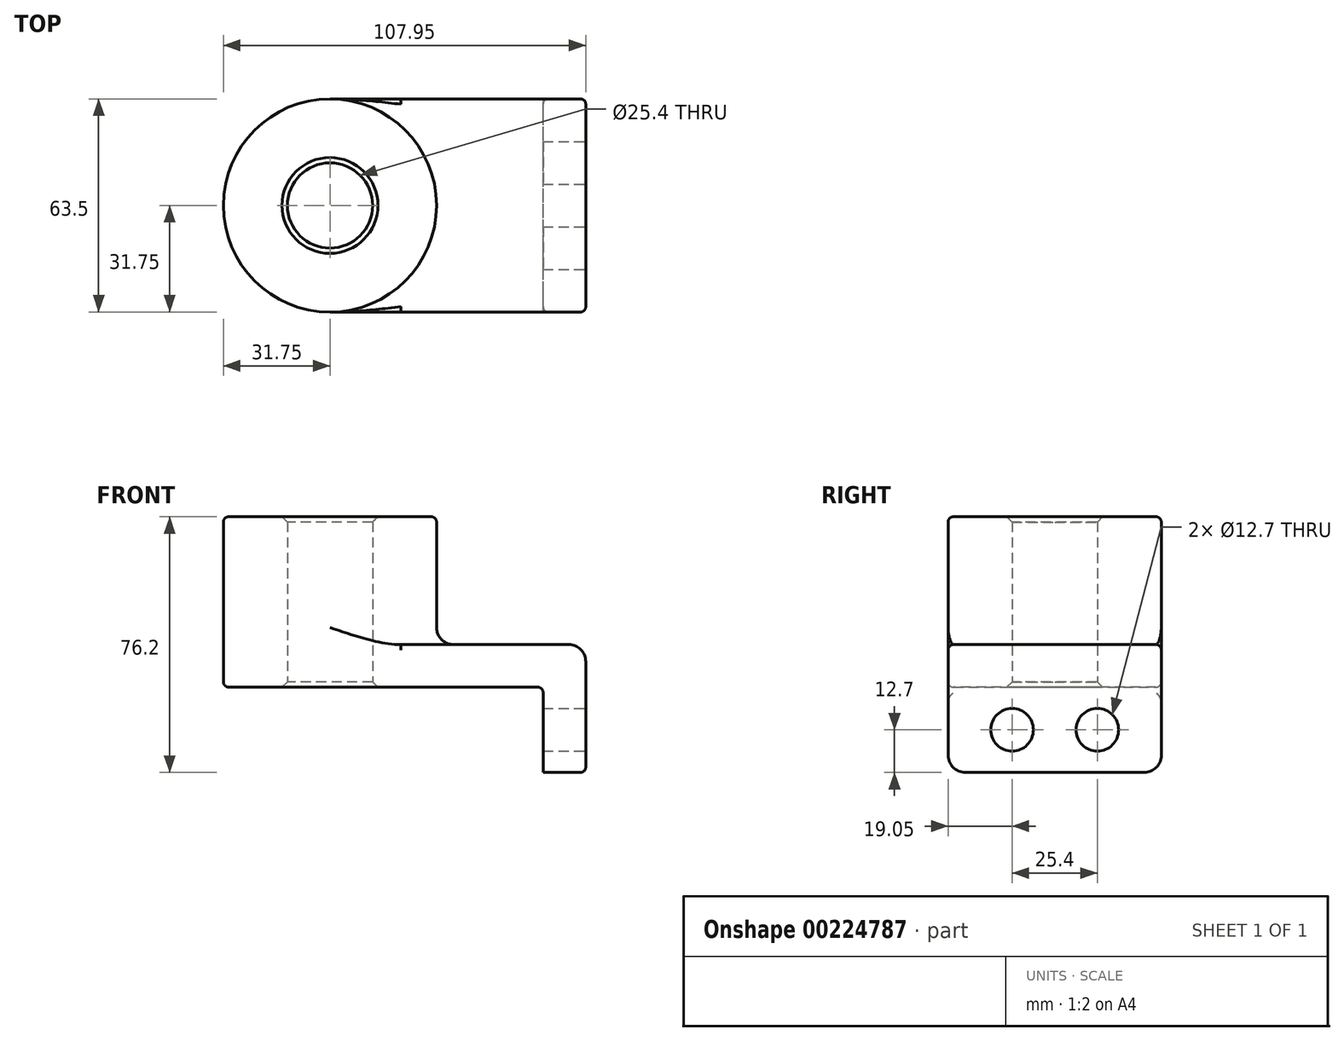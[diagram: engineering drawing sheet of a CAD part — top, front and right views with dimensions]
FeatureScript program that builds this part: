
annotation { "Feature Type Name" : "Feature", "Feature Type Description" : "" }
export const myFeature = defineFeature(function(context is Context, id is Id, definition is map)
    precondition{}
    {
        {
            var Q0;
            Q0=qCreatedBy(makeId("Top.planeOp"),FACE);
            var sketch = newSketch(context, id + "F0", { "sketchPlane" : qUnion([Q0])});
            skLineSegment(sketch, "E0.bottom", {"start": v(-38.1, 31.75) * mm, "end": v(38.1, 31.75) * mm});
            skLineSegment(sketch, "E0.top", {"start": v(-38.1, -31.75) * mm, "end": v(38.1, -31.75) * mm});
            skLineSegment(sketch, "E0.left", {"start": v(-38.1, 31.75) * mm, "end": v(-38.1, -31.75) * mm});
            skLineSegment(sketch, "E0.right", {"start": v(38.1, 31.75) * mm, "end": v(38.1, -31.75) * mm});
            skPoint(sketch, "E0.middle", {"position": v(0, 0) * mm});
            skCircle(sketch, "E1", {"center": v(-38.1, 0) * mm, "radius": 31.75 * mm});
            skCircle(sketch, "E2", {"center": v(-38.1, 0) * mm, "radius": 12.7 * mm});
            skSolve(sketch);
        }
        {
            var Q0;
            Q0 = qSketchRegion(id + "F0", true);
            extrude(context, id + "F1", {"entities" : qUnion([Q0]), "depth" : 12.7 * mm});
        }
        {
            var Q0;
            {var subQ1=sQuery(id+"F0.wireOp",EDGE,"E0.left");var subQ3=sQuery(id+"F0.wireOp",EDGE,"E2");var subQ4=makeQuery(id+"F0.imprint","INTERSECT",VERTEX,{"disambiguationData":[OD(0.0)],"derivedFrom":[subQ1,subQ3]});Q0=makeQuery(id+"F0.imprint","IMPRINT",FACE,{"disambiguationData":[TD([[makeQuery(id+"F0.imprint","IMPRINT",EDGE,{"disambiguationData":[TD([[subQ4,-1.0]])],"derivedFrom":subQ3}),-1.0]])]});}
            var Q1;
            {var subQ1=sQuery(id+"F0.wireOp",EDGE,"E0.left");var subQ3=sQuery(id+"F0.wireOp",EDGE,"E2");var subQ4=makeQuery(id+"F0.imprint","INTERSECT",VERTEX,{"disambiguationData":[OD(0.0)],"derivedFrom":[subQ1,subQ3]});Q1=makeQuery(id+"F0.imprint","IMPRINT",FACE,{"disambiguationData":[TD([[makeQuery(id+"F0.imprint","IMPRINT",EDGE,{"disambiguationData":[TD([[subQ4,1.0]])],"derivedFrom":subQ3}),-1.0]])]});}
            extrude(context, id + "F2", {"entities" : qUnion([Q0, Q1]), "operationType" : NewBodyOperationType.ADD, "depth" : 50.8 * mm});
        }
        {
            var Q0;
            Q0=makeQuery(id+"F1.opExtrude","SWEPT_FACE",FACE,{"disambiguationData":[OSD([sQuery(id+"F0.wireOp",EDGE,"E0.right")])]});
            var sketch = newSketch(context, id + "F3", { "sketchPlane" : qUnion([Q0])});
            skLineSegment(sketch, "E3.bottom", {"start": v(-31.75, 12.7) * mm, "end": v(31.75, 12.7) * mm});
            skLineSegment(sketch, "E3.top", {"start": v(-31.75, -25.4) * mm, "end": v(31.75, -25.4) * mm});
            skLineSegment(sketch, "E3.left", {"start": v(-31.75, 12.7) * mm, "end": v(-31.75, -25.4) * mm});
            skLineSegment(sketch, "E3.right", {"start": v(31.75, 12.7) * mm, "end": v(31.75, -25.4) * mm});
            skCircle(sketch, "E4", {"center": v(-12.7, -12.7) * mm, "radius": 6.35 * mm});
            skLineSegment(sketch, "E5", {"start": v(0, 0) * mm, "end": v(0, -25.4) * mm, "construction": true});
            skCircle(sketch, "E6.MirrorC", {"center": v(12.7, -12.7) * mm, "radius": 6.35 * mm});
            skSolve(sketch);
        }
        {
            var Q0;
            {var subQ2=sQuery(id+"F3.wireOp",EDGE,"E3.top");Q0=makeQuery(id+"F3.imprint","IMPRINT",FACE,{"disambiguationData":[TD([[makeQuery(id+"F3.imprint","IMPRINT",EDGE,{"derivedFrom":subQ2}),1.0]])]});}
            var Q1;
            {var subQ0=sQuery(id+"F3.wireOp",EDGE,"E3.bottom");Q1=makeQuery(id+"F3.imprint","IMPRINT",FACE,{"disambiguationData":[TD([[makeQuery(id+"F3.imprint","IMPRINT",EDGE,{"derivedFrom":subQ0}),1.0]])]});}
            extrude(context, id + "F4", {"entities" : qUnion([Q0, Q1]), "operationType" : NewBodyOperationType.ADD, "oppositeDirection" : true, "depth" : 12.7 * mm});
        }
        {
            var Q0;
            {var subQ0=sQuery(id+"F0.wireOp",EDGE,"E1");Q0=makeQuery(id+"F2.boolean.opBoolean","INTERSECT",EDGE,{"derivedFrom":[makeQuery(id+"F1.opExtrude","CAP_FACE",FACE,{"disambiguationData":[OSD([sQuery(id+"F0.wireOp",EDGE,"E0.bottom"),sQuery(id+"F0.wireOp",EDGE,"E0.top"),sQuery(id+"F0.wireOp",EDGE,"E0.right"),subQ0,sQuery(id+"F0.wireOp",EDGE,"E2")])],"isStart":false}),makeQuery(id+"F2.opExtrude","SWEPT_FACE",FACE,{"disambiguationData":[OSD([subQ0])]})]});}
            var Q1;
            Q1=makeQuery(id+"F1.opExtrude","CAP_EDGE",EDGE,{"disambiguationData":[OSD([sQuery(id+"F0.wireOp",EDGE,"E0.right")])],"isStart":false});
            var Q2;
            Q2=makeQuery(id+"F4.opExtrude","SWEPT_EDGE",EDGE,{"disambiguationData":[OSD([sQuery(id+"F3.wireOp",EDGE,"E3.top"),sQuery(id+"F3.wireOp",EDGE,"E3.left")])]});
            var Q3;
            Q3=makeQuery(id+"F4.opExtrude","SWEPT_EDGE",EDGE,{"disambiguationData":[OSD([sQuery(id+"F3.wireOp",EDGE,"E3.top"),sQuery(id+"F3.wireOp",EDGE,"E3.right")])]});
            fillet(context, id + "F5", {"entities" : qUnion([Q0, Q1, Q2, Q3]), "radius" : 5.08 * mm, "tangentPropagation" : true, "allowEdgeOverflow" : false});
        }
        {
            var Q0;
            Q0=makeQuery(id+"F1.opExtrude","CAP_EDGE",EDGE,{"disambiguationData":[OSD([sQuery(id+"F0.wireOp",EDGE,"E0.top")])],"isStart":false});
            var Q1;
            Q1=makeQuery(id+"F1.opExtrude","CAP_EDGE",EDGE,{"disambiguationData":[OSD([sQuery(id+"F0.wireOp",EDGE,"E0.top")])],"isStart":true});
            var Q2;
            Q2=makeQuery(id+"F4.boolean.opBoolean","INTERSECT",EDGE,{"derivedFrom":[makeQuery(id+"F1.opExtrude","CAP_FACE",FACE,{"disambiguationData":[OSD([sQuery(id+"F0.wireOp",EDGE,"E0.bottom"),sQuery(id+"F0.wireOp",EDGE,"E0.top"),sQuery(id+"F0.wireOp",EDGE,"E0.right"),sQuery(id+"F0.wireOp",EDGE,"E1"),sQuery(id+"F0.wireOp",EDGE,"E2")])],"isStart":true}),makeQuery(id+"F4.opExtrude","CAP_FACE",FACE,{"disambiguationData":[OSD([sQuery(id+"F3.wireOp",EDGE,"E3.bottom"),sQuery(id+"F3.wireOp",EDGE,"E3.top"),sQuery(id+"F3.wireOp",EDGE,"E3.left"),sQuery(id+"F3.wireOp",EDGE,"E3.right"),sQuery(id+"F3.wireOp",EDGE,"E4"),sQuery(id+"F3.wireOp",EDGE,"E6.MirrorC")])],"isStart":false})]});
            var Q3;
            Q3=makeQuery(id+"F2.opExtrude","CAP_EDGE",EDGE,{"disambiguationData":[OSD([sQuery(id+"F0.wireOp",EDGE,"E1")])],"isStart":false});
            fillet(context, id + "F6", {"entities" : qUnion([Q0, Q1, Q2, Q3]), "radius" : 1.59 * mm, "tangentPropagation" : true, "allowEdgeOverflow" : false});
        }
        {
            var Q0;
            {var subQ0=sQuery(id+"F0.wireOp",EDGE,"E2");Q0=makeQuery(id+"F2.boolean.opBoolean","MERGE",FACE,{"derivedFrom":[makeQuery(id+"F1.opExtrude","SWEPT_FACE",FACE,{"disambiguationData":[OSD([subQ0])]}),makeQuery(id+"F2.opExtrude","SWEPT_FACE",FACE,{"disambiguationData":[OSD([subQ0])]})]});}
            chamfer(context, id + "F7", {"entities" : qUnion([Q0]), "width" : 1.59 * mm, "tangentPropagation" : true});
        }
    });
